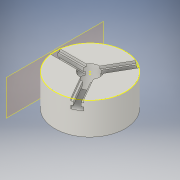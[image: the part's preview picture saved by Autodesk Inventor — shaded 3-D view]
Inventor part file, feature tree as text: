
AUTODESK INVENTOR PART (.ipt)
format: ipt  version: 2018 (Build 220112000, 112)  size: 259,072 bytes
history: native  units: in
note: dims shown in document units (in); Inventor stores cm internally (conversion verified against a paired STEP export)
features: sketch x13, extrude x11, plane x1, pattern_circular x1, projected_geometry x1
ambient origin geometry x8: Origin, YZ Plane, XZ Plane, XY Plane, X Axis, Y Axis, Z Axis, Center Point
bodies: Solid1 (feature_tree)
feature tree (27):
  extrude  "Extrusion1"  Depth=3.5787in
  extrude  "Extrusion2"  Depth=3.5787in
  sketch  "Sketch3"  dims[d13=1.1811in d15=360.0deg d17=0.2827in d18=0.0in]
  extrude  "Extrusion6"  Depth=0.2827in TaperAngle=0.0deg
  extrude  "Extrusion7"  Depth=0.3937in TaperAngle=0.0deg
  extrude  "Extrusion8"  Depth=0.3937in TaperAngle=0.0deg
  extrude  "Extrusion9"  Depth=0.3748in TaperAngle=0.0deg
  extrude  "Extrusion10"  Depth=0.3937in TaperAngle=0.0deg
  sketch  "Sketch12"  dims[d43=1.1811in d44=360.0deg d48=1.1811in d50=360.0deg]
  sketch  "Sketch13"  dims[d52=1.9685in d53=0.0in]
  plane  "Work Plane10"
  extrude  "Extrusion11"  Depth=1.1811in TaperAngle=360.0deg
  extrude  "Extrusion12"  [1 undecoded]
  extrude  "Extrusion13"  [1 undecoded]
  pattern_circular  "Circular Pattern1"  [2 undecoded]
  extrude  "Extrusion14"  [1 undecoded]
  sketch  "Sketch1"  dims[d1=3.5787in d2=0.0in d3=2.1701in]
  sketch  "Sketch2"  dims[d4=3.5787in d5=0.0in d6=0.5256in]
  sketch  "Sketch7"  dims[d19=0.3937in d20=0.0in d21=0.3937in d22=0.0in]
  sketch  "Sketch8"  dims[d23=0.3937in d24=0.0in d25=0.3937in d26=0.0in]
  sketch  "Sketch10"  dims[d36=0.3748in d37=2.9365in d38=0.0in]
  sketch  "Sketch11"  dims[d39=2.9365in d40=0.0in d41=0.3937in d42=0.0in]
  projected_geometry  "Projected Loop1"
  sketch  "Sketch16"
  sketch  "Sketch18"
  sketch  "Sketch20"
  sketch  "Sketch21"
note: 5 required parameter values undecoded (feature->parameter linkage not recoverable at this tier; creation-order binding heuristic only, values carry confidence <= 0.55)
